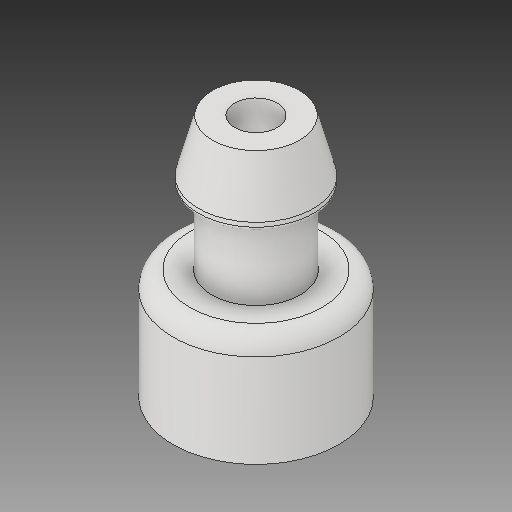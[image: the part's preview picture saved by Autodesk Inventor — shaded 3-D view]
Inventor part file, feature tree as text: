
AUTODESK INVENTOR PART (.ipt)
format: ipt  version: 2019 (Build 230136000, 136)  size: 162,816 bytes
history: native  units: in
note: dims shown in document units (in); Inventor stores cm internally (conversion verified against a paired STEP export)
features: fillet x1
ambient origin geometry x8: Origin, YZ Plane, XZ Plane, XY Plane, X Axis, Y Axis, Z Axis, Center Point
bodies: Solid1 (feature_tree)
feature tree (1):
  fillet  "Fillet1"  [1 undecoded]
note: 1 required parameter value undecoded (feature->parameter linkage not recoverable at this tier; creation-order binding heuristic only, values carry confidence <= 0.55)
